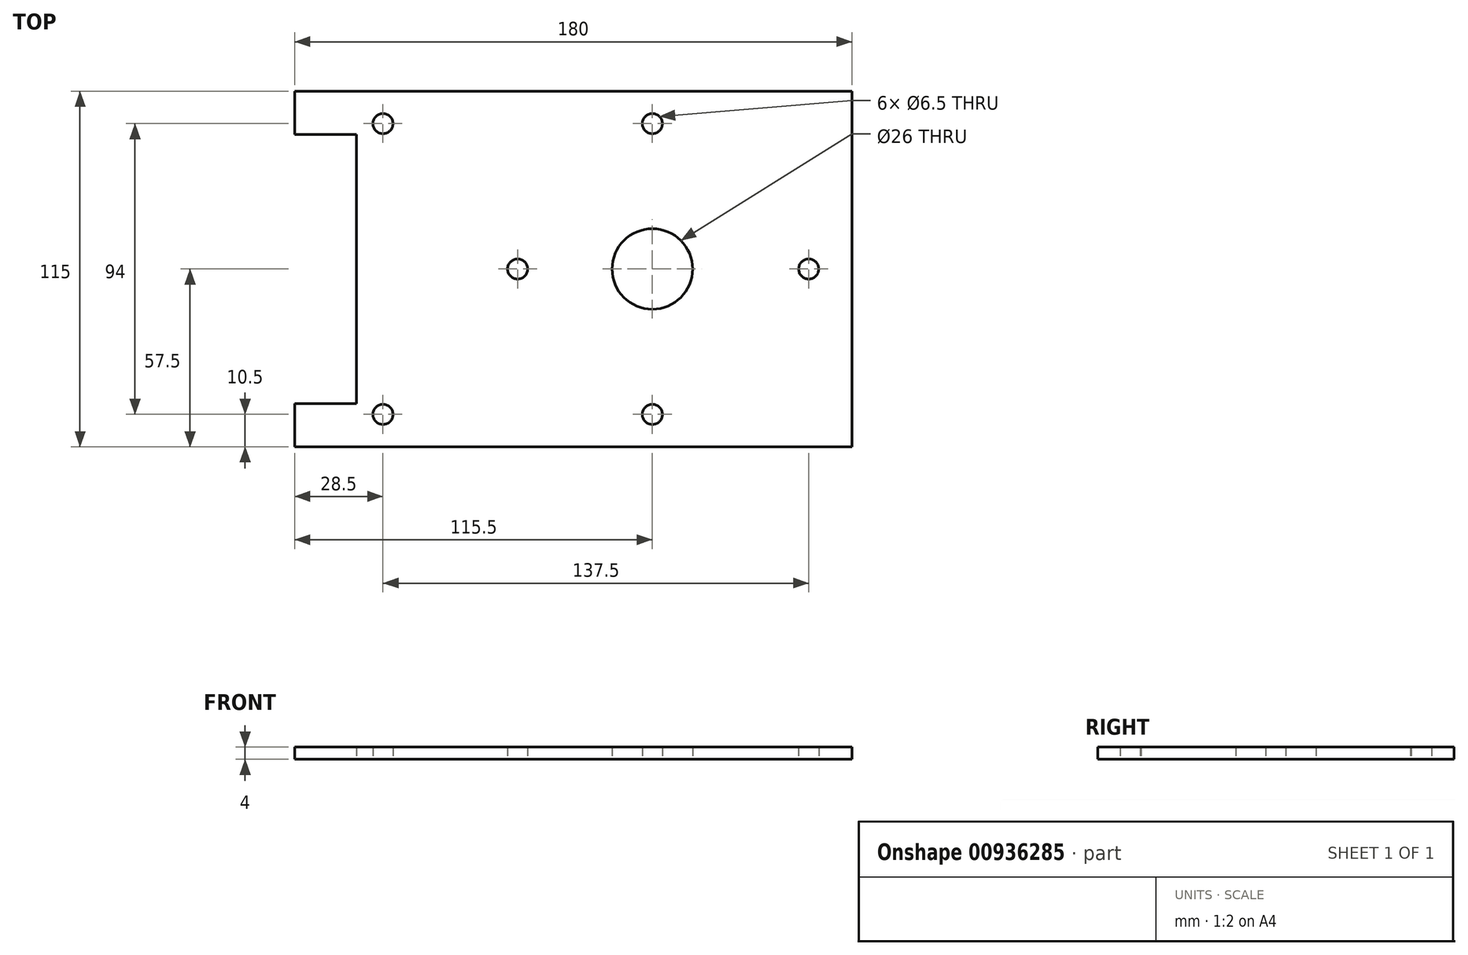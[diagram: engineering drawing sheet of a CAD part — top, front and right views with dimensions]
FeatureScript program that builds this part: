
annotation { "Feature Type Name" : "Feature", "Feature Type Description" : "" }
export const myFeature = defineFeature(function(context is Context, id is Id, definition is map)
    precondition{}
    {
        {
            var Q0;
            Q0=qCreatedBy(makeId("Top.planeOp"),FACE);
            var sketch = newSketch(context, id + "F0", { "sketchPlane" : qUnion([Q0])});
            skLineSegment(sketch, "E0.bottom", {"start": v(-90, 57.5) * mm, "end": v(90, 57.5) * mm});
            skLineSegment(sketch, "E0.top", {"start": v(-90, -57.5) * mm, "end": v(90, -57.5) * mm});
            skLineSegment(sketch, "E0.left", {"start": v(-90, 57.5) * mm, "end": v(-90, 43.5) * mm});
            skLineSegment(sketch, "E0.right", {"start": v(90, 57.5) * mm, "end": v(90, -57.5) * mm});
            skPoint(sketch, "E0.middle", {"position": v(0, 0) * mm});
            skLineSegment(sketch, "E1", {"start": v(-90, 43.5) * mm, "end": v(-70, 43.5) * mm});
            skLineSegment(sketch, "E2", {"start": v(-70, 43.5) * mm, "end": v(-70, -43.5) * mm});
            skLineSegment(sketch, "E3", {"start": v(-70, -43.5) * mm, "end": v(-90, -43.5) * mm});
            skLineSegment(sketch, "E4.trimOffspring", {"start": v(-90, -43.5) * mm, "end": v(-90, -57.5) * mm});
            skLineSegment(sketch, "E5", {"start": v(-66.68, 47) * mm, "end": v(-54.03, 47) * mm, "construction": true});
            skLineSegment(sketch, "E6", {"start": v(-68.86, -47) * mm, "end": v(-53.44, -47) * mm, "construction": true});
            skLineSegment(sketch, "E7", {"start": v(19.64, -47) * mm, "end": v(31.3, -47) * mm, "construction": true});
            skLineSegment(sketch, "E8", {"start": v(76, 14.24) * mm, "end": v(76, -17.87) * mm, "construction": true});
            skLineSegment(sketch, "E9", {"start": v(66.68, 0) * mm, "end": v(87.55, 0) * mm, "construction": true});
            skLineSegment(sketch, "E10", {"start": v(-18, 10.07) * mm, "end": v(-18, -14.97) * mm, "construction": true});
            skLineSegment(sketch, "E11", {"start": v(-34.02, 0) * mm, "end": v(25.5, 0) * mm, "construction": true});
            skLineSegment(sketch, "E12", {"start": v(-61.5, 54.16) * mm, "end": v(-61.5, 37.65) * mm, "construction": true});
            skLineSegment(sketch, "E13", {"start": v(-61.5, -38.74) * mm, "end": v(-61.5, -53.8) * mm, "construction": true});
            skLineSegment(sketch, "E14", {"start": v(25.5, -38.38) * mm, "end": v(25.5, -55.25) * mm, "construction": true});
            skLineSegment(sketch, "E15", {"start": v(25.5, 52.17) * mm, "end": v(25.5, 0) * mm, "construction": true});
            skPoint(sketch, "E16.orphan", {"position": v(-32.2, -47) * mm});
            skLineSegment(sketch, "E17", {"start": v(16.27, 47) * mm, "end": v(35.11, 47) * mm, "construction": true});
            skPoint(sketch, "E18.orphan", {"position": v(24.77, -47) * mm});
            skPoint(sketch, "E19.orphan", {"position": v(21.5, 47) * mm});
            skPoint(sketch, "E20.orphan", {"position": v(-61.5, 47) * mm});
            skCircle(sketch, "E21", {"center": v(-61.5, 47) * mm, "radius": 3.25 * mm});
            skCircle(sketch, "E22", {"center": v(25.5, 47) * mm, "radius": 3.25 * mm});
            skPoint(sketch, "E22.centerSnap0", {"position": v(25.5, 44.73) * mm});
            skCircle(sketch, "E23", {"center": v(-61.5, -47) * mm, "radius": 3.25 * mm});
            skCircle(sketch, "E24", {"center": v(-18, 0) * mm, "radius": 3.25 * mm});
            skPoint(sketch, "E24.centerSnap0", {"position": v(-18, -2.45) * mm});
            skCircle(sketch, "E25", {"center": v(25.5, -47) * mm, "radius": 3.25 * mm});
            skCircle(sketch, "E26", {"center": v(76, 0) * mm, "radius": 3.25 * mm});
            skPoint(sketch, "E27.orphan", {"position": v(25.5, 37.29) * mm});
            skCircle(sketch, "E28", {"center": v(25.5, 0) * mm, "radius": 13 * mm});
            skSolve(sketch);
        }
        {
            var Q0;
            Q0 = qSketchRegion(id + "F0", true);
            extrude(context, id + "F1", {"entities" : qUnion([Q0]), "depth" : 4 * mm, "offsetDistance" : 25 * mm});
        }
    });
